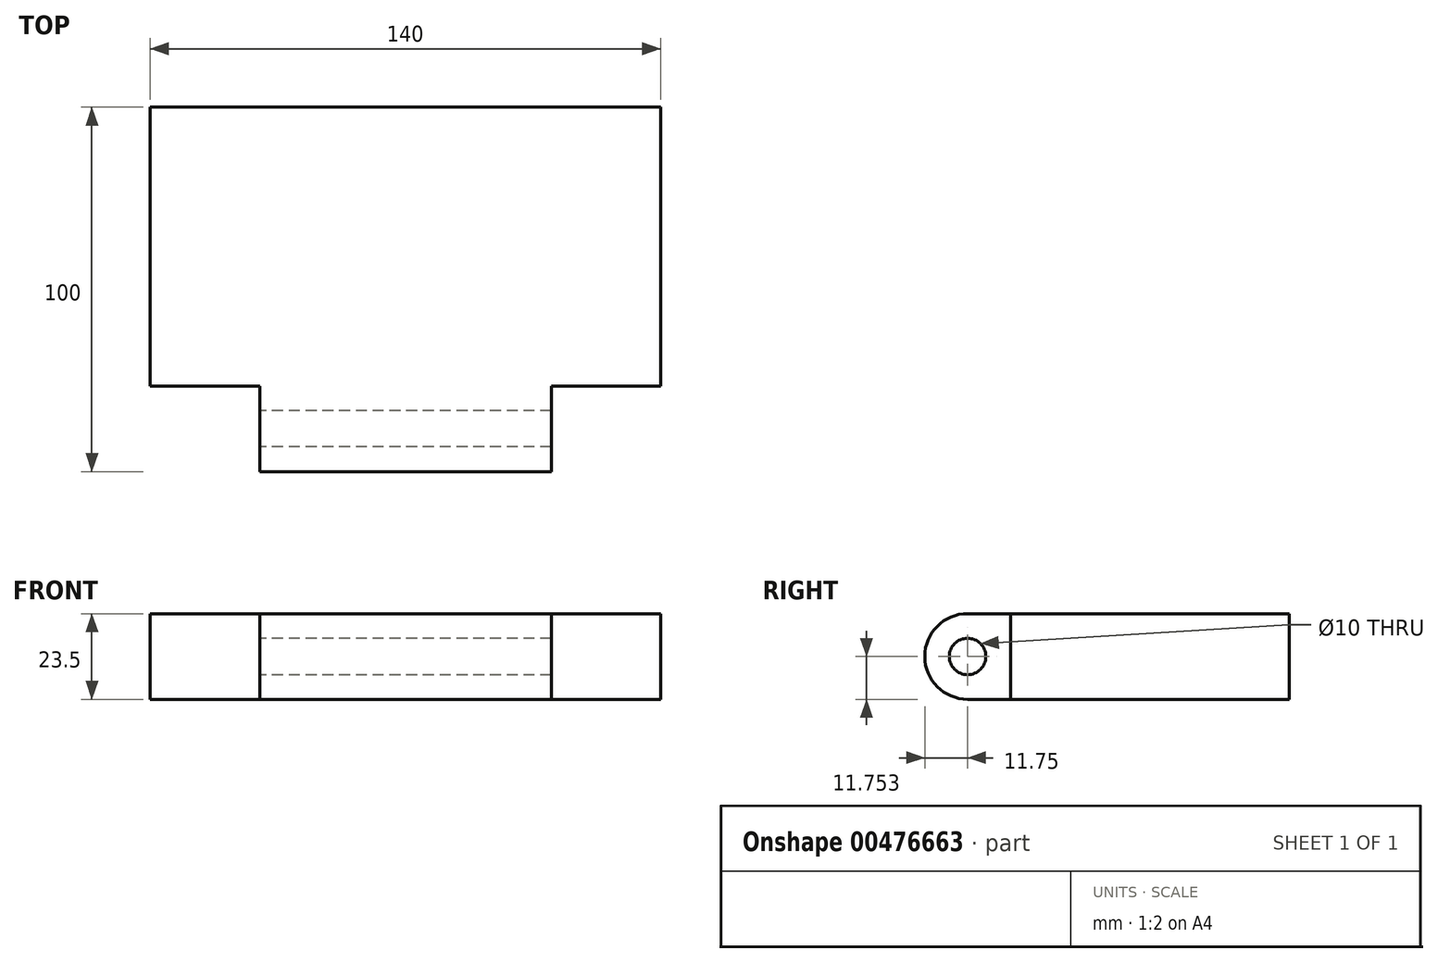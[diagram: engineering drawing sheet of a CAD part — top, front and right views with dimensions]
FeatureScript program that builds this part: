
annotation { "Feature Type Name" : "Feature", "Feature Type Description" : "" }
export const myFeature = defineFeature(function(context is Context, id is Id, definition is map)
    precondition{}
    {
        {
            var Q0;
            Q0=qCreatedBy(makeId("Front.planeOp"),FACE);
            var sketch = newSketch(context, id + "F0", { "sketchPlane" : qUnion([Q0])});
            skLineSegment(sketch, "E0.bottom", {"start": v(61.27, -8.09) * mm, "end": v(-78.73, -8.09) * mm});
            skLineSegment(sketch, "E0.top", {"start": v(61.27, -31.59) * mm, "end": v(-78.73, -31.59) * mm});
            skLineSegment(sketch, "E0.left", {"start": v(61.27, -8.09) * mm, "end": v(61.27, -31.59) * mm});
            skLineSegment(sketch, "E0.right", {"start": v(-78.73, -8.09) * mm, "end": v(-78.73, -31.59) * mm});
            skSolve(sketch);
        }
        {
            var Q0;
            Q0=qSketchRegion(id+"F0",true);
            extrude(context, id + "F1", {"entities" : qUnion([Q0]), "depth" : 50 * mm});
        }
        {
            var Q0;
            Q0=makeQuery(id+"F1.opExtrude","CAP_EDGE",EDGE,{"disambiguationData":[OSD([sQuery(id+"F0.wireOp",EDGE,"E0.bottom")])],"isStart":false});
            var Q1;
            Q1=makeQuery(id+"F1.opExtrude","CAP_EDGE",EDGE,{"disambiguationData":[OSD([sQuery(id+"F0.wireOp",EDGE,"E0.top")])],"isStart":false});
            fillet(context, id + "F2", {"entities" : qUnion([Q0, Q1]), "radius" : 11.75 * mm, "tangentPropagation" : true, "allowEdgeOverflow" : false});
        }
        {
            var Q0;
            Q0=makeQuery(id+"F1.opExtrude","SWEPT_FACE",FACE,{"disambiguationData":[OSD([sQuery(id+"F0.wireOp",EDGE,"E0.right")])]});
            var sketch = newSketch(context, id + "F3", { "sketchPlane" : qUnion([Q0])});
            skCircle(sketch, "E1", {"center": v(38.25, -19.84) * mm, "radius": 5 * mm});
            skSolve(sketch);
        }
        {
            var Q0;
            Q0=makeQuery(id+"F3.imprint","IMPRINT",FACE,{"disambiguationData":[TD([[makeQuery(id+"F3.imprint","IMPRINT",EDGE,{"derivedFrom":sQuery(id+"F3.wireOp",EDGE,"E1")}),1.0]])]});
            extrude(context, id + "F4", {"entities" : qUnion([Q0]), "operationType" : NewBodyOperationType.REMOVE, "endBound" : BoundingType.UP_TO_NEXT, "oppositeDirection" : true, "depth" : 25 * mm});
        }
        {
            var Q0;
            Q0=makeQuery(id+"F1.opExtrude","SWEPT_FACE",FACE,{"disambiguationData":[OSD([sQuery(id+"F0.wireOp",EDGE,"E0.top")])]});
            var sketch = newSketch(context, id + "F5", { "sketchPlane" : qUnion([Q0])});
            skLineSegment(sketch, "E2", {"start": v(-78.73, 38.25) * mm, "end": v(-78.73, 33.25) * mm});
            skLineSegment(sketch, "E3", {"start": v(-78.73, 33.25) * mm, "end": v(-78.73, 26.5) * mm});
            skPoint(sketch, "E4.firstSnap0", {"position": v(-8.73, 38.25) * mm});
            skLineSegment(sketch, "E4.right", {"start": v(-48.73, 51.5) * mm, "end": v(-48.73, 26.5) * mm});
            skLineSegment(sketch, "E5.right", {"start": v(31.27, 51.5) * mm, "end": v(31.27, 26.5) * mm});
            skLineSegment(sketch, "E6.bottom", {"start": v(-48.73, 26.5) * mm, "end": v(-82.73, 26.5) * mm});
            skLineSegment(sketch, "E6.top", {"start": v(-48.73, 66.32) * mm, "end": v(-82.73, 66.32) * mm});
            skLineSegment(sketch, "E6.left", {"start": v(-48.73, 26.5) * mm, "end": v(-48.73, 66.32) * mm});
            skLineSegment(sketch, "E6.right", {"start": v(-82.73, 26.5) * mm, "end": v(-82.73, 66.32) * mm});
            skLineSegment(sketch, "E7.bottom", {"start": v(31.27, 26.5) * mm, "end": v(74.63, 26.5) * mm});
            skLineSegment(sketch, "E7.top", {"start": v(31.27, 61.94) * mm, "end": v(74.63, 61.94) * mm});
            skLineSegment(sketch, "E7.left", {"start": v(31.27, 26.5) * mm, "end": v(31.27, 61.94) * mm});
            skLineSegment(sketch, "E7.right", {"start": v(74.63, 26.5) * mm, "end": v(74.63, 61.94) * mm});
            skSolve(sketch);
        }
        {
            var Q0;
            Q0=qSketchRegion(id+"F5",true);
            extrude(context, id + "F6", {"entities" : qUnion([Q0]), "operationType" : NewBodyOperationType.REMOVE, "oppositeDirection" : true, "depth" : 25 * mm});
        }
        {
            var Q0;
            Q0=makeQuery(id+"F1.opExtrude","CAP_FACE",FACE,{"disambiguationData":[OSD([sQuery(id+"F0.wireOp",EDGE,"E0.bottom"),sQuery(id+"F0.wireOp",EDGE,"E0.top"),sQuery(id+"F0.wireOp",EDGE,"E0.left"),sQuery(id+"F0.wireOp",EDGE,"E0.right")])],"isStart":true});
            var sketch = newSketch(context, id + "F7", { "sketchPlane" : qUnion([Q0])});
            skLineSegment(sketch, "E8.bottom", {"start": v(-61.27, -8.09) * mm, "end": v(78.73, -8.09) * mm});
            skLineSegment(sketch, "E8.top", {"start": v(-61.27, -31.59) * mm, "end": v(78.73, -31.59) * mm});
            skLineSegment(sketch, "E8.left", {"start": v(-61.27, -8.09) * mm, "end": v(-61.27, -31.59) * mm});
            skLineSegment(sketch, "E8.right", {"start": v(78.73, -8.09) * mm, "end": v(78.73, -31.59) * mm});
            skSolve(sketch);
        }
        {
            var Q0;
            Q0 = qSketchRegion(id + "F7", true);
            extrude(context, id + "F8", {"entities" : qUnion([Q0]), "operationType" : NewBodyOperationType.ADD, "depth" : 50 * mm});
        }
    });
